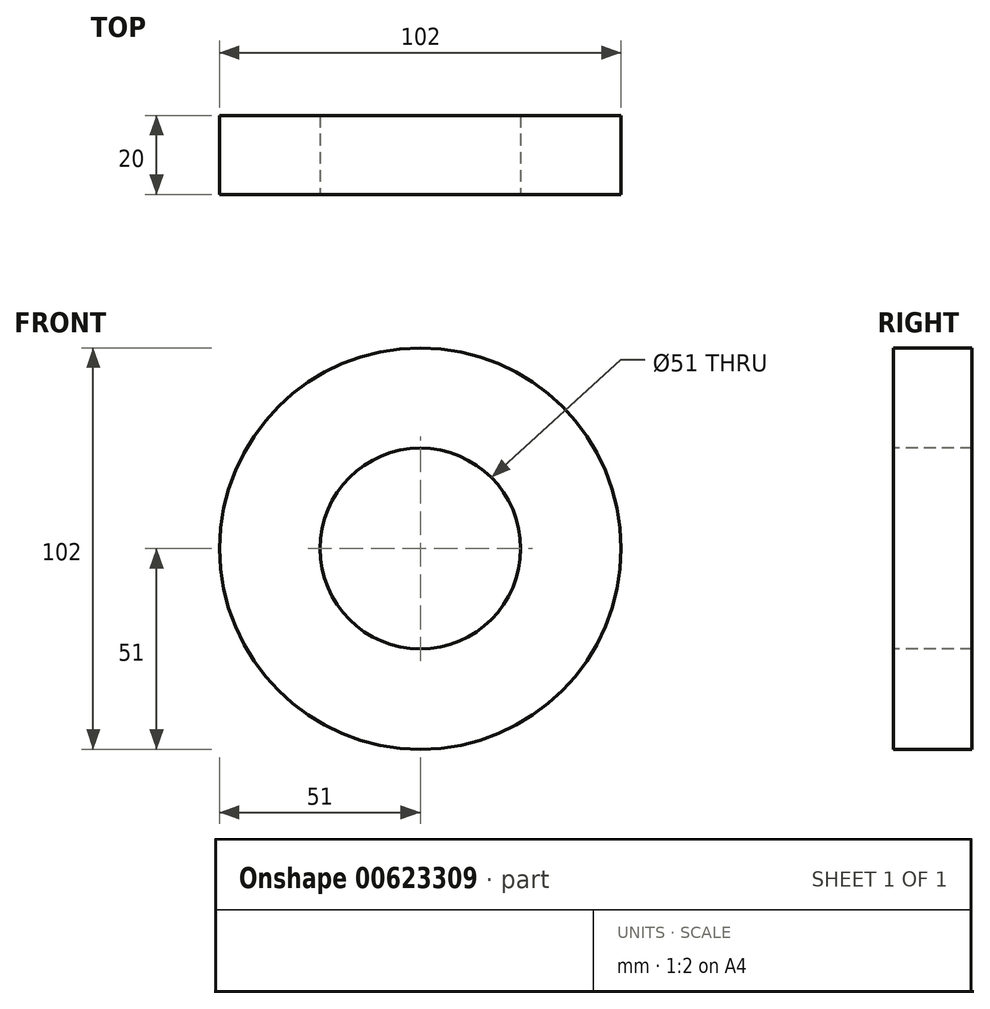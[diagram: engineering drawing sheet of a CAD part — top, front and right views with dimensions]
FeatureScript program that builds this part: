
annotation { "Feature Type Name" : "Feature", "Feature Type Description" : "" }
export const myFeature = defineFeature(function(context is Context, id is Id, definition is map)
    precondition{}
    {
        {
            var Q0;
            Q0=qCreatedBy(makeId("Front.planeOp"),FACE);
            var sketch = newSketch(context, id + "F0", { "sketchPlane" : qUnion([Q0])});
            skCircle(sketch, "E0", {"center": v(0, 0) * mm, "radius": 51 * mm});
            skSolve(sketch);
        }
        {
            var Q0;
            Q0 = qSketchRegion(id + "F0", true);
            extrude(context, id + "F1", {"entities" : qUnion([Q0]), "oppositeDirection" : true, "depth" : 20 * mm, "offsetDistance" : 25 * mm});
        }
        {
            var Q0;
            Q0=qCreatedBy(makeId("Front.planeOp"),FACE);
            var sketch = newSketch(context, id + "F2", { "sketchPlane" : qUnion([Q0])});
            skCircle(sketch, "E1", {"center": v(0, 0) * mm, "radius": 25.5 * mm});
            skSolve(sketch);
        }
        {
            var Q0;
            Q0=makeQuery(id+"F2.imprint","IMPRINT",FACE,{"disambiguationData":[TD([[makeQuery(id+"F2.imprint","IMPRINT",EDGE,{"derivedFrom":sQuery(id+"F2.wireOp",EDGE,"E1")}),1.0]])]});
            extrude(context, id + "F3", {"entities" : qUnion([Q0]), "operationType" : NewBodyOperationType.REMOVE, "oppositeDirection" : true, "depth" : 20 * mm, "offsetDistance" : 25 * mm});
        }
    });
